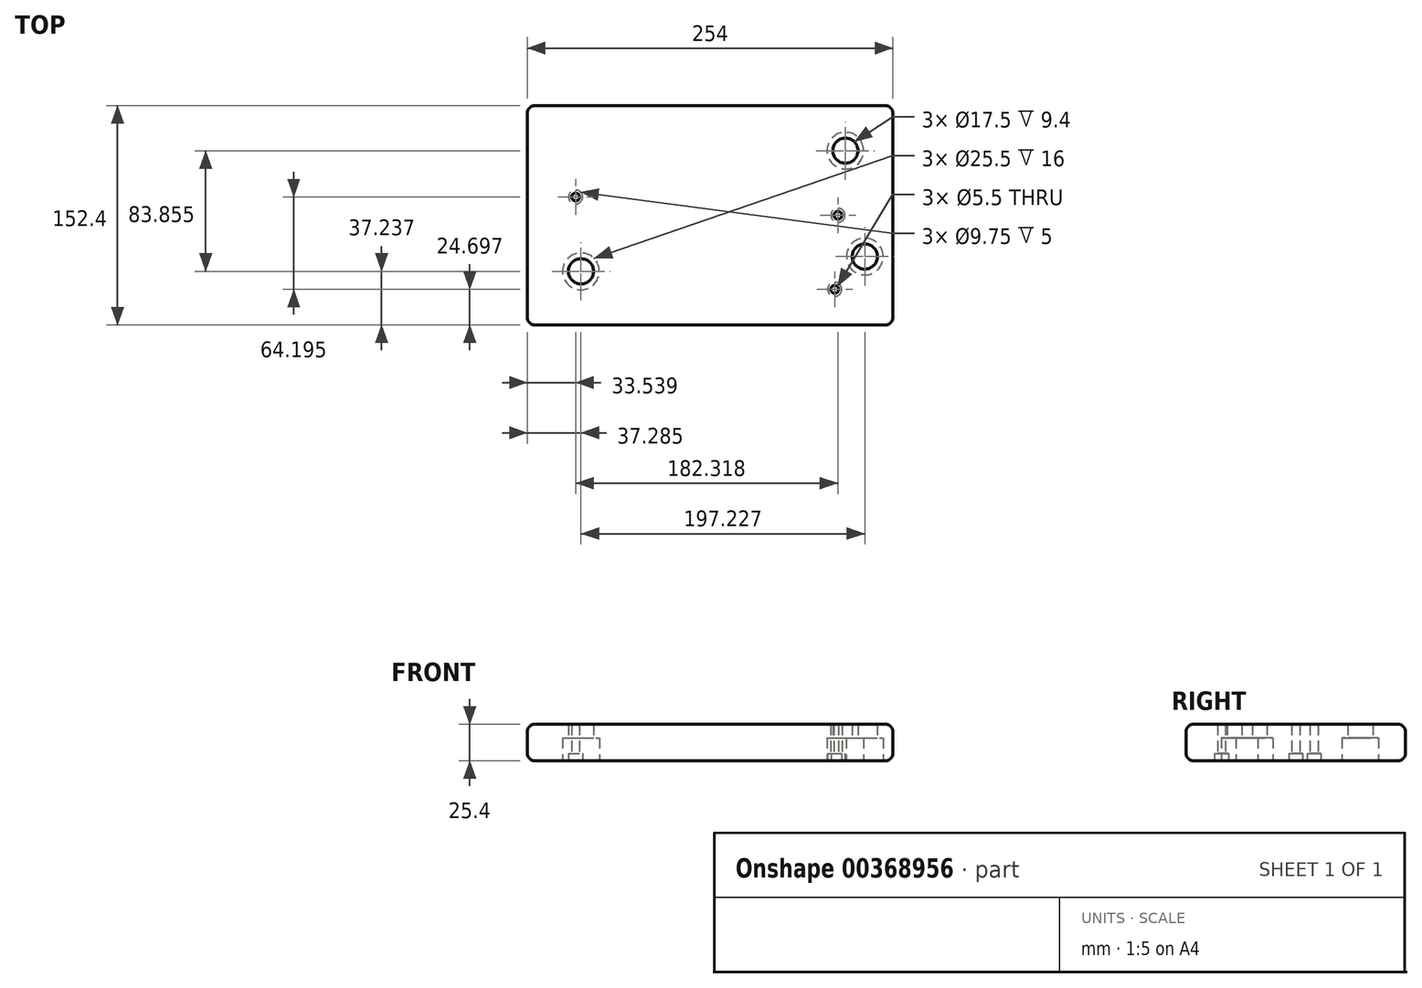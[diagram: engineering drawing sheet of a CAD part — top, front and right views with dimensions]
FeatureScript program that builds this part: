
annotation { "Feature Type Name" : "Feature", "Feature Type Description" : "" }
export const myFeature = defineFeature(function(context is Context, id is Id, definition is map)
    precondition{}
    {
        {
            var Q0;
            Q0=qCreatedBy(makeId("Top.planeOp"),FACE);
            var sketch = newSketch(context, id + "F0", { "sketchPlane" : qUnion([Q0])});
            skLineSegment(sketch, "E0.bottom", {"start": v(127, 76.2) * mm, "end": v(-127, 76.2) * mm});
            skLineSegment(sketch, "E0.top", {"start": v(127, -76.2) * mm, "end": v(-127, -76.2) * mm});
            skLineSegment(sketch, "E0.left", {"start": v(127, 76.2) * mm, "end": v(127, -76.2) * mm});
            skLineSegment(sketch, "E0.right", {"start": v(-127, 76.2) * mm, "end": v(-127, -76.2) * mm});
            skPoint(sketch, "E0.middle", {"position": v(0, 0) * mm});
            skSolve(sketch);
        }
        {
            var Q0;
            Q0=makeQuery(id+"F0.imprint","IMPRINT",FACE,{"disambiguationData":[TD([[makeQuery(id+"F0.imprint","IMPRINT",EDGE,{"derivedFrom":sQuery(id+"F0.wireOp",EDGE,"E0.bottom")}),1.0]])]});
            extrude(context, id + "F1", {"entities" : qUnion([Q0]), "depth" : 25.4 * mm});
        }
        {
            var Q0;
            Q0=makeQuery(id+"F1.opExtrude","CAP_FACE",FACE,{"disambiguationData":[OSD([sQuery(id+"F0.wireOp",EDGE,"E0.bottom"),sQuery(id+"F0.wireOp",EDGE,"E0.top"),sQuery(id+"F0.wireOp",EDGE,"E0.left"),sQuery(id+"F0.wireOp",EDGE,"E0.right")])],"isStart":false});
            var Q1;
            Q1=makeQuery(id+"F1.opExtrude","SWEPT_FACE",FACE,{"disambiguationData":[OSD([sQuery(id+"F0.wireOp",EDGE,"E0.bottom")])]});
            var Q2;
            Q2=makeQuery(id+"F1.opExtrude","SWEPT_EDGE",EDGE,{"disambiguationData":[OSD([sQuery(id+"F0.wireOp",EDGE,"E0.bottom"),sQuery(id+"F0.wireOp",EDGE,"E0.left")])]});
            var Q3;
            Q3=makeQuery(id+"F1.opExtrude","SWEPT_FACE",FACE,{"disambiguationData":[OSD([sQuery(id+"F0.wireOp",EDGE,"E0.left")])]});
            var Q4;
            Q4=makeQuery(id+"F1.opExtrude","SWEPT_FACE",FACE,{"disambiguationData":[OSD([sQuery(id+"F0.wireOp",EDGE,"E0.top")])]});
            var Q5;
            Q5=makeQuery(id+"F1.opExtrude","SWEPT_FACE",FACE,{"disambiguationData":[OSD([sQuery(id+"F0.wireOp",EDGE,"E0.right")])]});
            fillet(context, id + "F2", {"entities" : qUnion([Q0, Q1, Q2, Q3, Q4, Q5]), "radius" : 5.08 * mm, "tangentPropagation" : true, "allowEdgeOverflow" : false});
        }
        {
            var Q0;
            Q0=makeQuery(id+"F1.opExtrude","CAP_FACE",FACE,{"disambiguationData":[OSD([sQuery(id+"F0.wireOp",EDGE,"E0.bottom"),sQuery(id+"F0.wireOp",EDGE,"E0.top"),sQuery(id+"F0.wireOp",EDGE,"E0.left"),sQuery(id+"F0.wireOp",EDGE,"E0.right")])],"isStart":true});
            var sketch = newSketch(context, id + "F3", { "sketchPlane" : qUnion([Q0])});
            skPoint(sketch, "E1", {"position": v(-89.71, 38.96) * mm});
            skPoint(sketch, "E2", {"position": v(94.01, -44.9) * mm});
            skPoint(sketch, "E3", {"position": v(107.51, 28.69) * mm});
            skSolve(sketch);
        }
        {
            var Q0;
            Q0=sQuery(id+"F3.wireOp",VERTEX,"E3");
            var Q1;
            Q1=sQuery(id+"F3.wireOp",VERTEX,"E2");
            var Q2;
            Q2=sQuery(id+"F3.wireOp",VERTEX,"E1");
            var Q3;
            Q3=makeQuery(id+"F1.opExtrude","SWEPT_BODY",BODY,{"disambiguationData":[OSD([sQuery(id+"F0.wireOp",EDGE,"E0.bottom"),sQuery(id+"F0.wireOp",EDGE,"E0.top"),sQuery(id+"F0.wireOp",EDGE,"E0.left"),sQuery(id+"F0.wireOp",EDGE,"E0.right")])]});
            hole(context, id + "F4", {"style" : HoleStyle.C_BORE, "endStyle" : HoleEndStyle.THROUGH, "standardTappedOrClearance" : lookupTablePath({ "standard" : "ISO", "fit" : "Normal", "size" : "M16", "type" : "Clearance" }), "standardBlindInLast" : lookupTablePath({ "fit" : "Standard", "standard" : "ISO", "size" : "M16", "type" : "Clearance" }), "holeDiameter" : 17.5 * mm, "cBoreDiameter" : 25.5 * mm, "cBoreDepth" : 16 * mm, "isTappedThrough" : true, "tappedDepth" : 12.7 * mm, "tapClearance" : 3, "locations" : qUnion([Q0, Q1, Q2]), "scope" : qUnion([Q3])});
        }
        {
            var Q0;
            Q0=makeQuery(id+"F1.opExtrude","CAP_FACE",FACE,{"disambiguationData":[OSD([sQuery(id+"F0.wireOp",EDGE,"E0.bottom"),sQuery(id+"F0.wireOp",EDGE,"E0.top"),sQuery(id+"F0.wireOp",EDGE,"E0.left"),sQuery(id+"F0.wireOp",EDGE,"E0.right")])],"isStart":true});
            var sketch = newSketch(context, id + "F5", { "sketchPlane" : qUnion([Q0])});
            skPoint(sketch, "E4", {"position": v(47.6, 4.16) * mm});
            skPoint(sketch, "E5", {"position": v(88.86, 0) * mm});
            skPoint(sketch, "E6", {"position": v(86.58, 51.5) * mm});
            skPoint(sketch, "E7", {"position": v(-93.46, -12.7) * mm});
            skSolve(sketch);
        }
        {
            var Q0;
            Q0=sQuery(id+"F5.wireOp",VERTEX,"E7");
            var Q1;
            Q1=sQuery(id+"F5.wireOp",VERTEX,"E5");
            var Q2;
            Q2=sQuery(id+"F5.wireOp",VERTEX,"E6");
            var Q3;
            Q3=makeQuery(id+"F1.opExtrude","SWEPT_BODY",BODY,{"disambiguationData":[OSD([sQuery(id+"F0.wireOp",EDGE,"E0.bottom"),sQuery(id+"F0.wireOp",EDGE,"E0.top"),sQuery(id+"F0.wireOp",EDGE,"E0.left"),sQuery(id+"F0.wireOp",EDGE,"E0.right")])]});
            hole(context, id + "F6", {"style" : HoleStyle.C_BORE, "endStyle" : HoleEndStyle.THROUGH, "standardTappedOrClearance" : lookupTablePath({ "standard" : "ISO", "fit" : "Normal", "size" : "M5", "type" : "Clearance" }), "standardBlindInLast" : lookupTablePath({ "fit" : "Standard", "standard" : "ISO", "size" : "M5", "type" : "Clearance" }), "holeDiameter" : 5.5 * mm, "cBoreDiameter" : 9.75 * mm, "cBoreDepth" : 5 * mm, "isTappedThrough" : true, "tappedDepth" : 12.7 * mm, "tapClearance" : 3, "locations" : qUnion([Q0, Q1, Q2]), "scope" : qUnion([Q3])});
        }
    });
